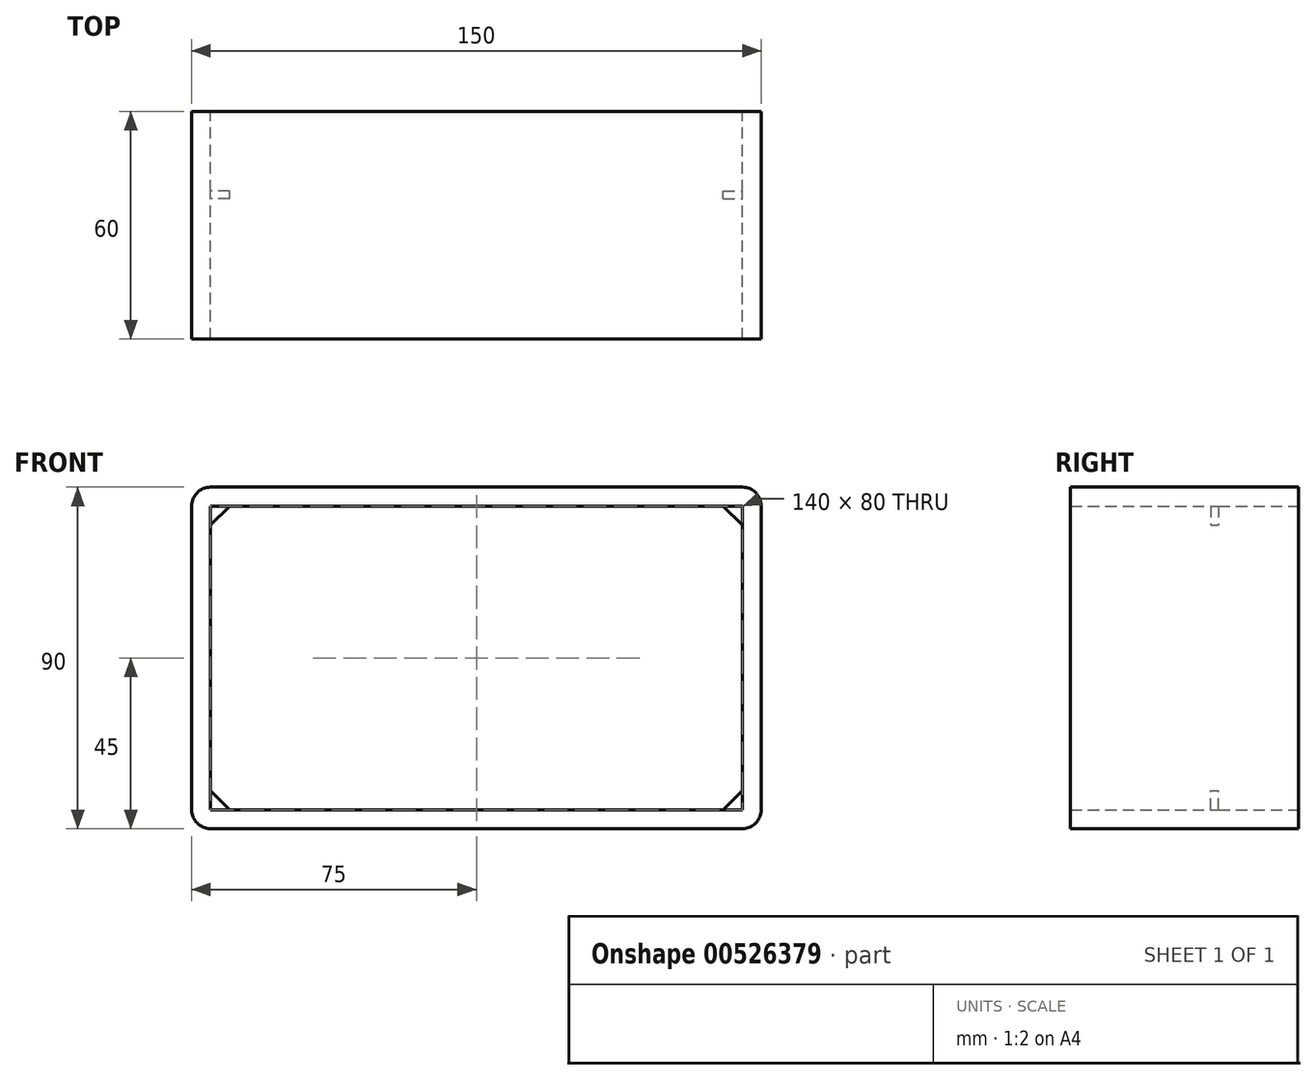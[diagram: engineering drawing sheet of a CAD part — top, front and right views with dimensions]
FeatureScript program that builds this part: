
annotation { "Feature Type Name" : "Feature", "Feature Type Description" : "" }
export const myFeature = defineFeature(function(context is Context, id is Id, definition is map)
    precondition{}
    {
        {
            var Q0;
            Q0=qCreatedBy(makeId("Front.planeOp"),FACE);
            var sketch = newSketch(context, id + "F0", { "sketchPlane" : qUnion([Q0])});
            skLineSegment(sketch, "E0.bottom", {"start": v(750, -450) * mm, "end": v(-750, -450) * mm});
            skLineSegment(sketch, "E0.top", {"start": v(750, 450) * mm, "end": v(-750, 450) * mm});
            skLineSegment(sketch, "E0.left", {"start": v(750, -450) * mm, "end": v(750, 450) * mm});
            skLineSegment(sketch, "E0.right", {"start": v(-750, -450) * mm, "end": v(-750, 450) * mm});
            skPoint(sketch, "E0.middle", {"position": v(0, 0) * mm});
            skLineSegment(sketch, "E1.0", {"start": v(-700, -400) * mm, "end": v(-700, 400) * mm});
            skLineSegment(sketch, "E1.1", {"start": v(700, -400) * mm, "end": v(-700, -400) * mm});
            skLineSegment(sketch, "E1.2", {"start": v(700, -400) * mm, "end": v(700, 400) * mm});
            skLineSegment(sketch, "E1.3", {"start": v(700, 400) * mm, "end": v(-700, 400) * mm});
            skSolve(sketch);
        }
        {
            var Q0;
            Q0 = qSketchRegion(id + "F0", true);
            extrude(context, id + "F1", {"entities" : qUnion([Q0]), "depth" : 600 * mm, "offsetDistance" : 25 * mm});
        }
        {
            var Q0;
            Q0=makeQuery(id+"F1.opExtrude","SWEPT_BODY",BODY,{"disambiguationData":[OSD([sQuery(id+"F0.wireOp",EDGE,"E0.bottom"),sQuery(id+"F0.wireOp",EDGE,"E0.top"),sQuery(id+"F0.wireOp",EDGE,"E0.left"),sQuery(id+"F0.wireOp",EDGE,"E0.right"),sQuery(id+"F0.wireOp",EDGE,"E1.0"),sQuery(id+"F0.wireOp",EDGE,"E1.1"),sQuery(id+"F0.wireOp",EDGE,"E1.2"),sQuery(id+"F0.wireOp",EDGE,"E1.3")])]});
            var Q1;
            Q1=qCreatedBy(makeId("Origin.pointOp"),VERTEX);
            transform(context, id + "F2", {"entities" : qUnion([Q0]), "transformType" : TransformType.SCALE_UNIFORMLY, "scale" : .1, "scalePoint" : qUnion([Q1]), "makeCopy" : false});
        }
        {
            var Q0;
            Q0=makeQuery(id+"F1.opExtrude","CAP_FACE",FACE,{"disambiguationData":[OSD([sQuery(id+"F0.wireOp",EDGE,"E0.bottom"),sQuery(id+"F0.wireOp",EDGE,"E0.top"),sQuery(id+"F0.wireOp",EDGE,"E0.left"),sQuery(id+"F0.wireOp",EDGE,"E0.right"),sQuery(id+"F0.wireOp",EDGE,"E1.0"),sQuery(id+"F0.wireOp",EDGE,"E1.1"),sQuery(id+"F0.wireOp",EDGE,"E1.2"),sQuery(id+"F0.wireOp",EDGE,"E1.3")])],"isStart":true});
            cPlane(context, id + "F3", {"entities" : qUnion([Q0]), "cplaneType" : CPlaneType.OFFSET, "offset" : 14 * mm, "oppositeDirection" : true, "width" : 150 * mm, "height" : 150 * mm});
        }
        {
            var Q0;
            Q0=qCreatedBy(id+"F3.planeOp",FACE);
            cPlane(context, id + "F4", {"entities" : qUnion([Q0]), "cplaneType" : CPlaneType.OFFSET, "offset" : 7 * mm, "oppositeDirection" : true, "width" : 150 * mm, "height" : 150 * mm});
        }
        {
            var Q0;
            Q0=qCreatedBy(id+"F4.planeOp",FACE);
            var sketch = newSketch(context, id + "F5", { "sketchPlane" : qUnion([Q0])});
            skLineSegment(sketch, "E2", {"start": v(0, 0) * mm, "end": v(0, 25.32) * mm, "construction": true});
            skLineSegment(sketch, "E3", {"start": v(-70, 40) * mm, "end": v(-70, 35) * mm});
            skLineSegment(sketch, "E4", {"start": v(-70, 35) * mm, "end": v(-65, 40) * mm});
            skLineSegment(sketch, "E5", {"start": v(-65, 40) * mm, "end": v(-70, 40) * mm});
            skLineSegment(sketch, "E6", {"start": v(0, 0) * mm, "end": v(-15.28, 0) * mm, "construction": true});
            skLineSegment(sketch, "E7.MirrorCS", {"start": v(70, 35) * mm, "end": v(65, 40) * mm});
            skLineSegment(sketch, "E8.MirrorCS", {"start": v(65, 40) * mm, "end": v(70, 40) * mm});
            skLineSegment(sketch, "E9.MirrorCS", {"start": v(70, 40) * mm, "end": v(70, 35) * mm});
            skLineSegment(sketch, "E10.MirrorCS", {"start": v(-70, -40) * mm, "end": v(-70, -35) * mm});
            skLineSegment(sketch, "E11.MirrorCS", {"start": v(-70, -35) * mm, "end": v(-65, -40) * mm});
            skLineSegment(sketch, "E12.MirrorCS", {"start": v(-65, -40) * mm, "end": v(-70, -40) * mm});
            skLineSegment(sketch, "E13.MirrorCS", {"start": v(70, -40) * mm, "end": v(70, -35) * mm});
            skLineSegment(sketch, "E14.MirrorCS", {"start": v(65, -40) * mm, "end": v(70, -40) * mm});
            skLineSegment(sketch, "E15.MirrorCS", {"start": v(70, -35) * mm, "end": v(65, -40) * mm});
            skSolve(sketch);
        }
        {
            var Q0;
            Q0 = qSketchRegion(id + "F5", true);
            extrude(context, id + "F6", {"entities" : qUnion([Q0]), "operationType" : NewBodyOperationType.ADD, "oppositeDirection" : true, "depth" : 2 * mm, "offsetDistance" : 25 * mm});
        }
        {
            var Q0;
            Q0=makeQuery(id+"F1.opExtrude","SWEPT_EDGE",EDGE,{"disambiguationData":[OSD([sQuery(id+"F0.wireOp",EDGE,"E0.top"),sQuery(id+"F0.wireOp",EDGE,"E0.left")])]});
            var Q1;
            Q1=makeQuery(id+"F1.opExtrude","SWEPT_EDGE",EDGE,{"disambiguationData":[OSD([sQuery(id+"F0.wireOp",EDGE,"E0.bottom"),sQuery(id+"F0.wireOp",EDGE,"E0.left")])]});
            var Q2;
            Q2=makeQuery(id+"F1.opExtrude","SWEPT_EDGE",EDGE,{"disambiguationData":[OSD([sQuery(id+"F0.wireOp",EDGE,"E0.bottom"),sQuery(id+"F0.wireOp",EDGE,"E0.right")])]});
            var Q3;
            Q3=makeQuery(id+"F1.opExtrude","SWEPT_EDGE",EDGE,{"disambiguationData":[OSD([sQuery(id+"F0.wireOp",EDGE,"E0.top"),sQuery(id+"F0.wireOp",EDGE,"E0.right")])]});
            fillet(context, id + "F7", {"entities" : qUnion([Q0, Q1, Q2, Q3]), "radius" : 5 * mm, "tangentPropagation" : true, "allowEdgeOverflow" : false});
        }
    });
